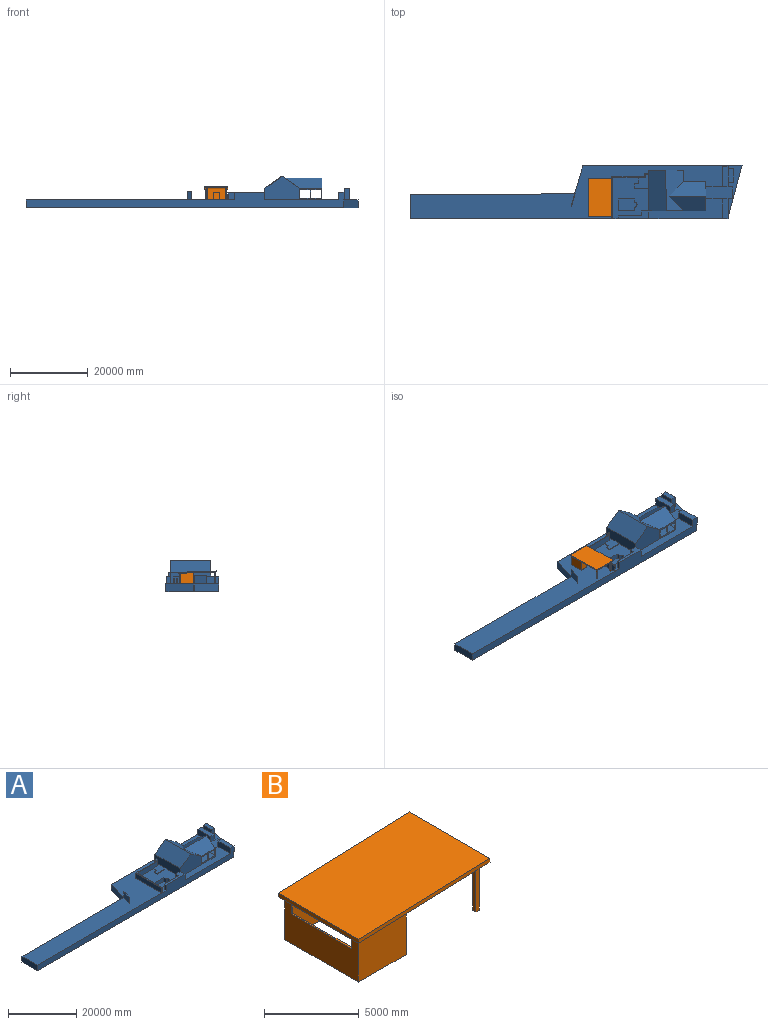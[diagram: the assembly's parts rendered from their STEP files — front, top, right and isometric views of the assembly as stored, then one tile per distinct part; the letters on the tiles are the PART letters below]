
ASSEMBLY  parts=2 mates=1
PART A: 98 faces, bbox 85423.7x13776x8103.6 mm
  f0: plane 806.34x800.03mm, normal (0,0,1), area 5093.9mm2, adj f3,f54,f55,f90,f91
  f1: plane 10574.56x9355.88mm, normal (0,0,1), area 68833319.2mm2, adj f2,f18,f26,f27,f28,f29,f30,f31
  f2: plane 10432.73x3000mm, normal (-1,-0.01,0), area 30163746mm2, adj f1,f4,f11,f25,f47,f53,f59,f60
  f3: plane 200x6.37mm, normal (-0.01,1,0), area 1273.4mm2, adj f0,f55,f59,f90
  f4: plane 85423.7x13775.99mm, normal (0,0,1), area 490703525.2mm2, adj f2,f10,f14,f15,f16,f17,f18,f19
  f5: plane 2200x200mm, normal (1,0,0), area 440000mm2, adj f10,f68,f70,f73
  f6: plane 2200x200mm, normal (-1,0,0), area 440000mm2, adj f10,f68,f70,f78
  f7: plane 2200x200mm, normal (1,0,0), area 440000mm2, adj f10,f68,f70,f75
  f8: plane 2200x200mm, normal (-1,0,0), area 440000mm2, adj f10,f68,f70,f73
  f9: plane 5800.4x3000mm, normal (0,-1,0), area 5740323.2mm2, adj f11,f13,f15,f63,f66,f67,f68,f69
  f10: plane 5800.4x3000mm, normal (0,1,0), area 5740323.2mm2, adj f4,f5,f6,f7,f8,f15,f23,f65
  f11: plane 8864.49x6103.59mm, normal (0.01,-1,0), area 40330864.7mm2, adj f2,f9,f13,f48,f60,f61,f62
  f12: plane 4154x10mm, normal (0,-1,0), area 41540mm2, adj f13,f15,f36,f45
  f13: plane 18809.03x5144mm, normal (0,0,1), area 51394512.7mm2, adj f9,f11,f12,f15,f18,f45,f48
  f14: plane 4154x10mm, normal (0,1,0), area 41540mm2, adj f4,f15,f36,f39
  f15: plane 7442.03x5605.48mm, normal (1,0,0), area 16498017.6mm2, adj f4,f9,f10,f12,f13,f14,f36,f63
  f16: plane 42374.08x2000mm, normal (0,1,0), area 84748620.8mm2, adj f4,f17,f21,f22
  f17: plane 6259.84x2000mm, normal (-1,0,0), area 12519675.8mm2, adj f4,f16,f18,f22
  f18: plane 81832.56x4000mm, normal (0,-1,0), area 182648538.8mm2, adj f1,f4,f13,f17,f19,f22,f42,f44
  f19: plane 13775.99x3683.7mm, normal (0.97,-0.26,0), area 28520000mm2, adj f4,f18,f20,f22,f42
  f20: plane 40949.62x2000mm, normal (0,1,0), area 81900000mm2, adj f4,f19,f21,f22
  f21: plane 7200x2100mm, normal (-0.96,0.28,0), area 15000000mm2, adj f4,f16,f20,f22
  f22: plane 85423.7x13775.99mm, normal (0,0,-1), area 824369427.1mm2, adj f16,f17,f18,f19,f20,f21
  f23: plane 3000x58.76mm, normal (-0.01,1,0), area 176296.3mm2, adj f4,f10,f24,f64
  f24: plane 3000x2991.17mm, normal (1,0.01,0), area 8973775.2mm2, adj f4,f23,f25,f62,f64
  f25: plane 8864.49x6103.59mm, normal (-0.01,1,0), area 40350606.9mm2, adj f2,f4,f24,f61,f62
  f26: plane 4160x1300mm, normal (0,-1,0), area 5408000mm2, adj f1,f27,f31,f32
  f27: plane 3010x1300mm, normal (1,0,0), area 3913000mm2, adj f1,f26,f28,f32
  f28: plane 4160x1300mm, normal (0,1,0), area 5408000mm2, adj f1,f27,f29,f32
  f29: plane 1300x905mm, normal (-1,0,0), area 1176500mm2, adj f1,f28,f30,f32
  f30: cylinder r=600mm len=1300mm, axis (0,0,1), area 2450442.3mm2, adj f1,f29,f31,f32
  f31: plane 1300x905mm, normal (-1,0,0), area 1176500mm2, adj f1,f26,f30,f32
  f32: plane 4760x3010mm, normal (0,0,1), area 13087086.7mm2, adj f26,f27,f28,f29,f30,f31
  f33: plane 1208x10mm, normal (0,1,0), area 12080mm2, adj f4,f35,f36,f40
  f34: plane 1208x10mm, normal (0,-1,0), area 12080mm2, adj f4,f35,f36,f44
  f35: plane 3064x10mm, normal (1,0,0), area 30640mm2, adj f4,f33,f34,f36
  f36: plane 6894x3064mm, normal (0,0,1), area 21123216mm2, adj f12,f14,f15,f33,f34,f35,f37,f43
  f37: plane 1990x1532mm, normal (0,-1,0), area 3048680mm2, adj f36,f39,f40,f41
  f38: plane 2000x1532mm, normal (0,1,0), area 3064000mm2, adj f4,f39,f40,f41
  f39: plane 5253.32x2000mm, normal (-1,0,0), area 10506631mm2, adj f4,f14,f37,f38,f41
  f40: plane 5253.32x2000mm, normal (1,0,0), area 10506631mm2, adj f4,f33,f37,f38,f41
  f41: plane 5253.32x1532mm, normal (0,0,1), area 8048079.4mm2, adj f37,f38,f39,f40
  f42: plane 346.15x92.56mm, normal (0,0,-1), area 16020.2mm2, adj f18,f19,f44
  f43: plane 1990x1532mm, normal (0,1,0), area 3048680mm2, adj f36,f44,f45,f46
  f44: plane 5144x2000mm, normal (1,0,0), area 10288000mm2, adj f4,f18,f34,f42,f43,f46
  f45: plane 5144x2000mm, normal (-1,0,0), area 10288000mm2, adj f12,f13,f18,f43,f46
  f46: plane 5144x1532mm, normal (0,0,1), area 7880608mm2, adj f18,f43,f44,f45
  f47: plane 2000x1890.11mm, normal (0,1,0), area 3780212.3mm2, adj f1,f2,f50,f60
  f48: plane 2000.08x2000mm, normal (1,0,0), area 4000155.9mm2, adj f11,f13,f18,f60
  f49: plane 2000x750mm, normal (-1,0,0), area 1500000mm2, adj f1,f18,f51,f60
  f50: plane 2000x1252.91mm, normal (-1,0,0), area 2505829.3mm2, adj f1,f47,f51,f60
  f51: plane 5940.77x2000mm, normal (0,1,0), area 11881538.8mm2, adj f1,f49,f50,f60
  f52: plane 1199.96x200mm, normal (-1,-0.01,0), area 240000mm2, adj f1,f53,f58,f59
  f53: plane 3699.88x200mm, normal (0.01,-1,0), area 740000mm2, adj f1,f2,f52,f59
  f54: plane 799.98x200mm, normal (-0.01,1,0), area 160000mm2, adj f0,f55,f59,f91
  f55: plane 799.98x200mm, normal (-1,-0.01,0), area 160000mm2, adj f0,f3,f54,f59
  f56: plane 1598.58x200mm, normal (-0.01,1,0), area 319725.1mm2, adj f1,f57,f59,f89
  f57: plane 1532.82x200mm, normal (-1,-0.01,0), area 306574.4mm2, adj f1,f56,f58,f59
  f58: plane 1059.97x200mm, normal (-0.01,1,0), area 212000mm2, adj f1,f52,f57,f59
  f59: plane 3709.36x3561.98mm, normal (0,0,1), area 9126564mm2, adj f2,f3,f52,f53,f54,f55,f56,f57
  f60: plane 7840.77x2002.91mm, normal (0,0,1), area 8261086.5mm2, adj f2,f11,f18,f47,f48,f49,f50,f51
  f61: plane 10467.73x4514.63mm, normal (-0.57,0,0.82), area 56452655.9mm2, adj f2,f11,f25,f62
  f62: plane 10467.73x4514.63mm, normal (0.57,0,0.82), area 39549350.8mm2, adj f11,f24,f25,f61,f63,f65
  f63: plane 9550.92x3721.01mm, normal (0,-0.57,0.82), area 34866837.7mm2, adj f9,f15,f62,f65
  f64: plane 58.77x0.46mm, normal (0,0,-1), area 13.6mm2, adj f23,f24,f65
  f65: plane 9550.92x3721.01mm, normal (0,0.57,0.82), area 35000313.4mm2, adj f10,f15,f62,f63,f64
  f66: plane 2200x200mm, normal (1,0,0), area 440000mm2, adj f9,f68,f70,f72
  f67: plane 2200x200mm, normal (-1,0,0), area 440000mm2, adj f9,f68,f70,f77
  f68: plane 7442.03x5857.59mm, normal (0,0,-1), area 43173689.3mm2, adj f5,f6,f7,f8,f9,f10,f15,f66
  f69: plane 2200x200mm, normal (1,0,0), area 440000mm2, adj f9,f68,f70,f76
  f70: plane 7442.03x5857.59mm, normal (0,0,1), area 43173689.3mm2, adj f5,f6,f7,f8,f9,f10,f15,f66
  f71: plane 2200x200mm, normal (-1,0,0), area 440000mm2, adj f9,f68,f70,f72
  f72: plane 2200x200mm, normal (0,1,0), area 440000mm2, adj f66,f68,f70,f71
  f73: plane 2200x200mm, normal (0,-1,0), area 440000mm2, adj f5,f8,f68,f70
  f74: plane 7042.03x2200mm, normal (1,0.01,0), area 15492944.6mm2, adj f68,f70,f75,f76
  f75: plane 2200x157.19mm, normal (0,-1,0), area 345813.4mm2, adj f7,f68,f70,f74
  f76: plane 2200x101.58mm, normal (0,1,0), area 223474.5mm2, adj f68,f69,f70,f74
  f77: plane 2200x200mm, normal (0,1,0), area 440000mm2, adj f15,f67,f68,f70
  f78: plane 2200x200mm, normal (0,-1,0), area 440000mm2, adj f6,f15,f68,f70
  f79: plane 2100x96mm, normal (0.28,0.96,0), area 210000mm2, adj f4,f80,f82,f83
  f80: plane 3208.8x2100mm, normal (-0.96,0.28,0), area 7019239.7mm2, adj f4,f79,f81,f83
  f81: plane 2100x96mm, normal (-0.28,-0.96,0), area 210000mm2, adj f4,f80,f82,f83
  f82: plane 3208.8x2100mm, normal (0.96,-0.28,0), area 7019239.7mm2, adj f4,f79,f81,f83
  f83: plane 3236.8x1031.9mm, normal (0,0,1), area 334249.5mm2, adj f79,f80,f81,f82
  f84: plane 1800x1033.17mm, normal (0,1,0), area 1859704.6mm2, adj f2,f4,f85,f92
  f85: plane 11617.76x9516.81mm, normal (0,0,1), area 4911180.4mm2, adj f2,f18,f84,f86,f87,f88,f89,f90
  f86: plane 8481.78x1800mm, normal (0,1,0), area 15267205.8mm2, adj f4,f85,f87,f92
  f87: plane 10809.56x1800mm, normal (-1,0,0), area 19457214.5mm2, adj f4,f18,f85,f86
  f88: plane 10574.56x1800mm, normal (1,0,0), area 19034214.5mm2, adj f1,f18,f85,f89
  f89: plane 8481.78x1800mm, normal (0,-1,0), area 15220205.8mm2, adj f1,f56,f59,f85,f88,f90
  f90: plane 1800x808.2mm, normal (1,0,0), area 1454385.6mm2, adj f0,f3,f59,f85,f89,f91
  f91: plane 1800x800.03mm, normal (0,-1,0), area 1440044.9mm2, adj f0,f2,f54,f85,f90
  f92: plane 1800x808.2mm, normal (-1,0,0), area 1454756.8mm2, adj f4,f84,f85,f86
  f93: plane 3000x1391.52mm, normal (0,1,0), area 4174551.3mm2, adj f4,f94,f96,f97
  f94: plane 3452.98x3000mm, normal (-1,0,0), area 10358938.3mm2, adj f4,f93,f95,f97
  f95: plane 3000x1391.52mm, normal (0,-1,0), area 4174551.3mm2, adj f4,f94,f96,f97
  f96: plane 3452.98x3000mm, normal (1,0,0), area 10358938.3mm2, adj f4,f93,f95,f97
  f97: plane 3452.98x1391.52mm, normal (0,0,1), area 4804879.9mm2, adj f93,f94,f95,f96
PART B: 33 faces, bbox 9808.7x6000x3342.2 mm
  f0: plane 5500x2882.85mm, normal (1,0,0), area 12510081.7mm2, adj f2,f12,f13,f14,f16,f17,f18
  f1: plane 5300x2879.36mm, normal (-1,0,0), area 11915003.4mm2, adj f8,f10,f14,f15,f16,f17,f18
  f2: plane 9800x6000mm, normal (0.03,0,-1), area 39125847.6mm2, adj f0,f4,f5,f6,f7,f11,f12,f13
  f3: plane 9800x6000mm, normal (-0.03,0,1), area 58835841.2mm2, adj f4,f5,f6,f7
  f4: plane 6000x249.85mm, normal (-1,0,-0.03), area 1500000mm2, adj f2,f3,f6,f7
  f5: plane 6000x249.85mm, normal (1,0,0.03), area 1500000mm2, adj f2,f3,f6,f7
  f6: plane 9808.73x592.07mm, normal (0,1,0), area 2451493.4mm2, adj f2,f3,f4,f5
  f7: plane 9808.73x592.07mm, normal (0,-1,0), area 2451493.4mm2, adj f2,f3,f4,f5
  f8: plane 3358.73x2879.36mm, normal (0,1,0), area 9474004mm2, adj f1,f9,f14,f15
  f9: plane 5300x2762.07mm, normal (1,0,0), area 11938970.4mm2, adj f8,f10,f14,f15,f19,f20,f21,f22
  f10: plane 3358.73x2879.36mm, normal (0,-1,0), area 9474004mm2, adj f1,f9,f14,f15
  f11: plane 5500x2758.58mm, normal (-1,0,0), area 12472177.9mm2, adj f2,f12,f13,f14,f19,f20,f21,f22
  f12: plane 3558.73x2882.85mm, normal (0,-1,0), area 10038146.9mm2, adj f0,f2,f11,f14
  f13: plane 3558.73x2882.85mm, normal (0,1,0), area 10038146.9mm2, adj f0,f2,f11,f14
  f14: plane 5500x3558.73mm, normal (0,0,-1), area 1607745mm2, adj f0,f1,f8,f9,f10,f11,f12,f13
  f15: plane 5300x3358.73mm, normal (0.03,0,-1), area 17812092.5mm2, adj f1,f8,f9,f10
  f16: plane 1640x100mm, normal (0,0,-1), area 164000mm2, adj f0,f1,f17,f18
  f17: plane 2040x100mm, normal (0,1,0), area 204000mm2, adj f0,f1,f14,f16
  f18: plane 2040x100mm, normal (0,-1,0), area 204000mm2, adj f0,f1,f14,f16
  f19: plane 600x100mm, normal (0,-1,0), area 60000mm2, adj f9,f11,f20,f21
  f20: plane 4500x100mm, normal (0,0,-1), area 450000mm2, adj f9,f11,f19,f22
  f21: plane 4500x100mm, normal (0,0,1), area 450000mm2, adj f9,f11,f19,f22
  f22: plane 600x100mm, normal (0,1,0), area 60000mm2, adj f9,f11,f20,f21
  f23: plane 3069.68x250mm, normal (-1,0,0), area 767419.3mm2, adj f2,f24,f26,f27
  f24: plane 3078.41x250mm, normal (0,-1,0), area 768510.6mm2, adj f2,f23,f25,f27
  f25: plane 3078.41x250mm, normal (1,0,0), area 769601.9mm2, adj f2,f24,f26,f27
  f26: plane 3078.41x250mm, normal (0,1,0), area 768510.6mm2, adj f2,f23,f25,f27
  f27: plane 250x250mm, normal (0,0,-1), area 62500mm2, adj f23,f24,f25,f26
  f28: plane 3069.68x250mm, normal (-1,0,0), area 767419.3mm2, adj f2,f29,f31,f32
  f29: plane 3078.41x250mm, normal (0,-1,0), area 768510.6mm2, adj f2,f28,f30,f32
  f30: plane 3078.41x250mm, normal (1,0,0), area 769601.9mm2, adj f2,f29,f31,f32
  f31: plane 3078.41x250mm, normal (0,1,0), area 768510.6mm2, adj f2,f28,f30,f32
  f32: plane 250x250mm, normal (0,0,-1), area 62500mm2, adj f28,f29,f30,f31
PLACE A t=(-39389.96,4839.94,1815.38)mm fixed
PLACE B rot(axis=(0,0,-1),90deg) t=(6550.81,15148.67,1815.38)mm
MATE fastened B.f32 <-> A.f4  axis (0,0,1) through (12150.81,5739.94,1815.38)mm
